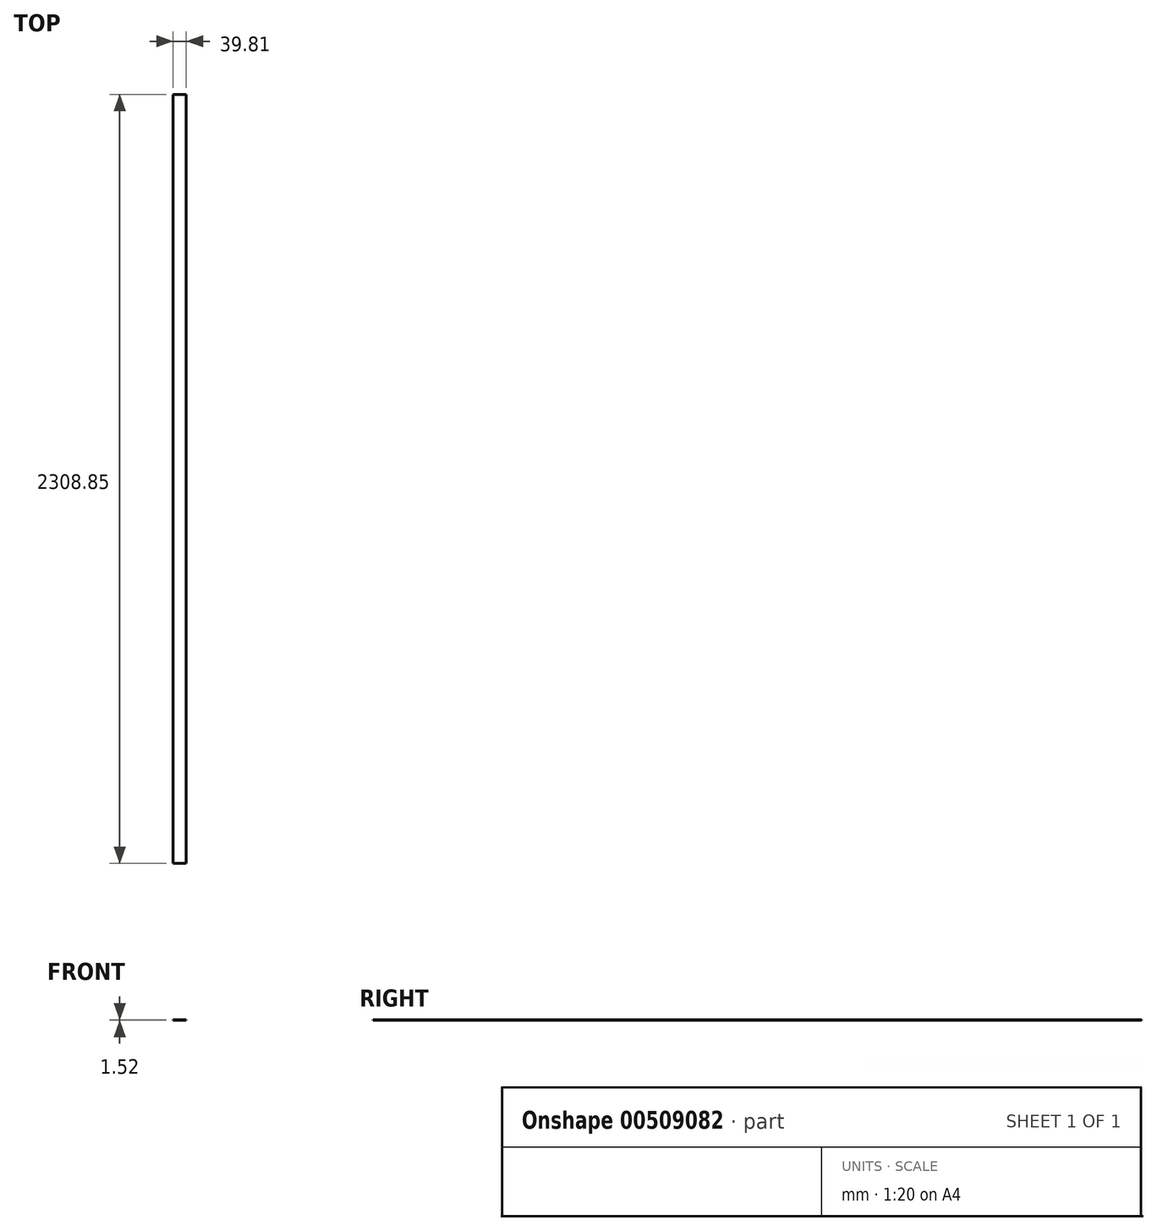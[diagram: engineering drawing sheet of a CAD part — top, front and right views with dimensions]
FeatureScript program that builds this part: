
annotation { "Feature Type Name" : "Feature", "Feature Type Description" : "" }
export const myFeature = defineFeature(function(context is Context, id is Id, definition is map)
    precondition{}
    {
        {
            var Q0;
            Q0=qCreatedBy(makeId("Front.planeOp"),FACE);
            var sketch = newSketch(context, id + "F0", { "sketchPlane" : qUnion([Q0])});
            skLineSegment(sketch, "E0", {"start": v(87.33, -165.55) * mm, "end": v(127.14, -165.55) * mm});
            skLineSegment(sketch, "E1", {"start": v(87.33, -164.03) * mm, "end": v(127.14, -164.03) * mm});
            skLineSegment(sketch, "E2", {"start": v(87.33, -164.03) * mm, "end": v(87.33, -165.55) * mm});
            skLineSegment(sketch, "E3", {"start": v(127.14, -165.55) * mm, "end": v(127.14, -164.03) * mm});
            skSolve(sketch);
        }
        {
            var Q0;
            Q0=makeQuery(id+"F0.imprint","IMPRINT",FACE,{"disambiguationData":[TD([[makeQuery(id+"F0.imprint","IMPRINT",EDGE,{"derivedFrom":sQuery(id+"F0.wireOp",EDGE,"E0")}),1.0]])]});
            extrude(context, id + "F1", {"entities" : qUnion([Q0]), "depth" : 2308.85 * mm});
        }
    });
